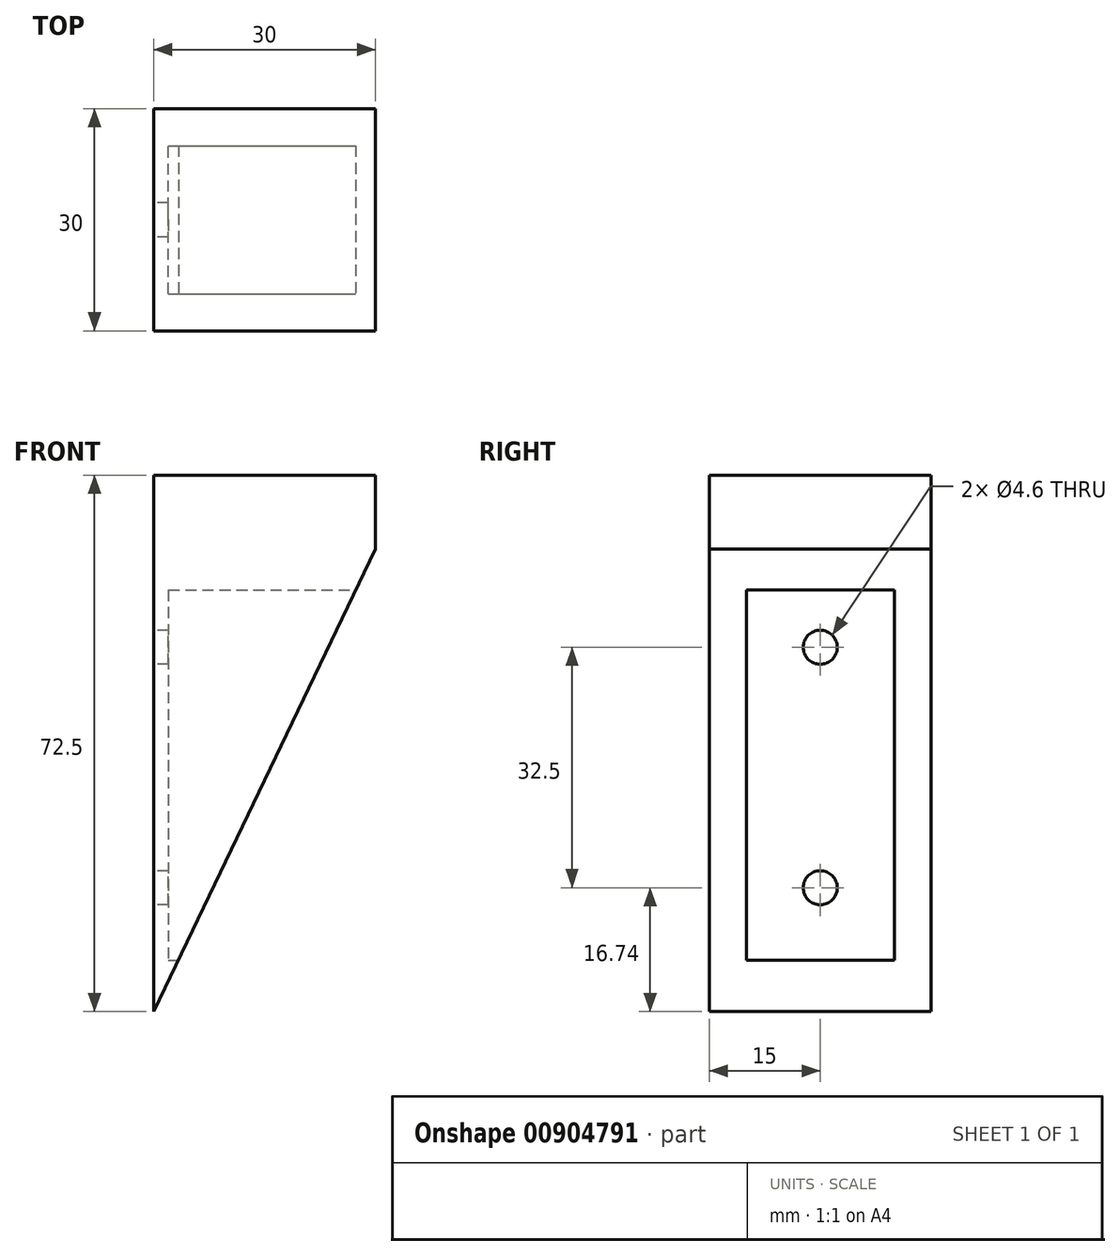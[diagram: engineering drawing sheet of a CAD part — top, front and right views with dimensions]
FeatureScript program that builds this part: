
annotation { "Feature Type Name" : "Feature", "Feature Type Description" : "" }
export const myFeature = defineFeature(function(context is Context, id is Id, definition is map)
    precondition{}
    {
        {
            var Q0;
            Q0=qCreatedBy(makeId("Front.planeOp"),FACE);
            var sketch = newSketch(context, id + "F0", { "sketchPlane" : qUnion([Q0])});
            skLineSegment(sketch, "E0", {"start": v(-15, 23.26) * mm, "end": v(15, 23.26) * mm});
            skLineSegment(sketch, "E1", {"start": v(-15, 23.26) * mm, "end": v(-15, -49.24) * mm});
            skLineSegment(sketch, "E2", {"start": v(15, 23.26) * mm, "end": v(15, 13.26) * mm});
            skLineSegment(sketch, "E3", {"start": v(15, 13.26) * mm, "end": v(-15, 13.26) * mm});
            skLineSegment(sketch, "E4", {"start": v(-15, -49.24) * mm, "end": v(15, 13.26) * mm});
            skSolve(sketch);
        }
        {
            var Q0;
            {var subQ0=sQuery(id+"F0.wireOp",EDGE,"E0");Q0=makeQuery(id+"F0.imprint","IMPRINT",FACE,{"disambiguationData":[TD([[makeQuery(id+"F0.imprint","IMPRINT",EDGE,{"derivedFrom":subQ0}),-1.0]])]});}
            var Q1;
            {var subQ2=sQuery(id+"F0.wireOp",EDGE,"E3");Q1=makeQuery(id+"F0.imprint","IMPRINT",FACE,{"disambiguationData":[TD([[makeQuery(id+"F0.imprint","IMPRINT",EDGE,{"derivedFrom":subQ2}),1.0]])]});}
            extrude(context, id + "F1", {"entities" : qUnion([Q0, Q1]), "depth" : 30 * mm, "offsetDistance" : 25 * mm});
        }
        {
            var Q0;
            Q0=makeQuery(id+"F1.opExtrude","SWEPT_FACE",FACE,{"disambiguationData":[OSD([sQuery(id+"F0.wireOp",EDGE,"E1")])]});
            var sketch = newSketch(context, id + "F2", { "sketchPlane" : qUnion([Q0])});
            skCircle(sketch, "E5", {"center": v(15, 0) * mm, "radius": 2.3 * mm});
            skCircle(sketch, "E6", {"center": v(15, -32.5) * mm, "radius": 2.3 * mm});
            skSolve(sketch);
        }
        {
            var Q0;
            Q0=makeQuery(id+"F2.imprint","IMPRINT",FACE,{"disambiguationData":[TD([[makeQuery(id+"F2.imprint","IMPRINT",EDGE,{"derivedFrom":sQuery(id+"F2.wireOp",EDGE,"E5")}),1.0]])]});
            var Q1;
            Q1=makeQuery(id+"F2.imprint","IMPRINT",FACE,{"disambiguationData":[TD([[makeQuery(id+"F2.imprint","IMPRINT",EDGE,{"derivedFrom":sQuery(id+"F2.wireOp",EDGE,"E6")}),1.0]])]});
            extrude(context, id + "F3", {"entities" : qUnion([Q0, Q1]), "operationType" : NewBodyOperationType.REMOVE, "endBound" : BoundingType.THROUGH_ALL, "oppositeDirection" : true, "depth" : 25 * mm, "offsetDistance" : 25 * mm});
        }
        {
            var Q0;
            Q0=qCreatedBy(makeId("Right.planeOp"),FACE);
            var sketch = newSketch(context, id + "F4", { "sketchPlane" : qUnion([Q0])});
            skLineSegment(sketch, "E7.bottom", {"start": v(-25, 7.73) * mm, "end": v(-5, 7.73) * mm});
            skLineSegment(sketch, "E7.top", {"start": v(-25, -42.27) * mm, "end": v(-5, -42.27) * mm});
            skLineSegment(sketch, "E7.left", {"start": v(-25, 7.73) * mm, "end": v(-25, -42.27) * mm});
            skLineSegment(sketch, "E7.right", {"start": v(-5, 7.73) * mm, "end": v(-5, -42.27) * mm});
            skSolve(sketch);
        }
        {
            var Q0;
            Q0=makeQuery(id+"F4.imprint","IMPRINT",FACE,{"disambiguationData":[TD([[makeQuery(id+"F4.imprint","IMPRINT",EDGE,{"derivedFrom":sQuery(id+"F4.wireOp",EDGE,"E7.bottom")}),-1.0]])]});
            extrude(context, id + "F5", {"entities" : qUnion([Q0]), "operationType" : NewBodyOperationType.REMOVE, "oppositeDirection" : true, "depth" : 13 * mm, "offsetDistance" : 25 * mm, "hasSecondDirection" : true, "secondDirectionBound" : SecondDirectionBoundingType.THROUGH_ALL, "secondDirectionOppositeDirection" : false, "secondDirectionDepth" : 25 * mm});
        }
    });
